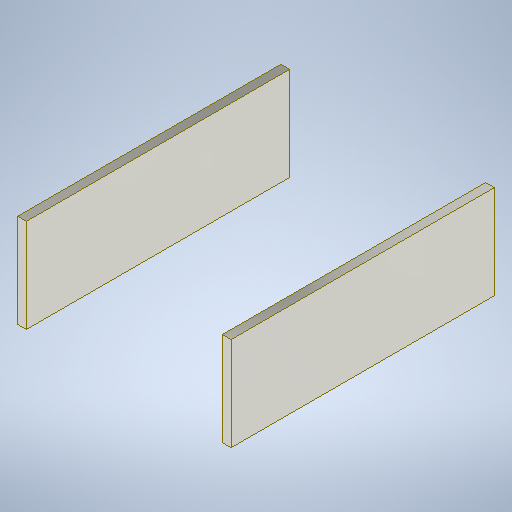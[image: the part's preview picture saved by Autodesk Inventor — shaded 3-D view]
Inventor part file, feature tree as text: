
AUTODESK INVENTOR PART (.ipt)
format: ipt  version: 2025.1 (Build 291241000, 241)  size: 237,568 bytes
history: native  units: mm
features: extrude x1, sketch x1
ambient origin geometry x8: Origin, YZ Plane, XZ Plane, XY Plane, X Axis, Y Axis, Z Axis, Center Point
bodies: Solid1 (feature_tree)
feature tree (2):
  extrude  "Extrusion1"  Depth=3.0mm
  sketch  "Sketch1"  dims[d0=73.0mm d1=3.0mm d2=32.0mm d3=16.0mm d5=0.0mm]
